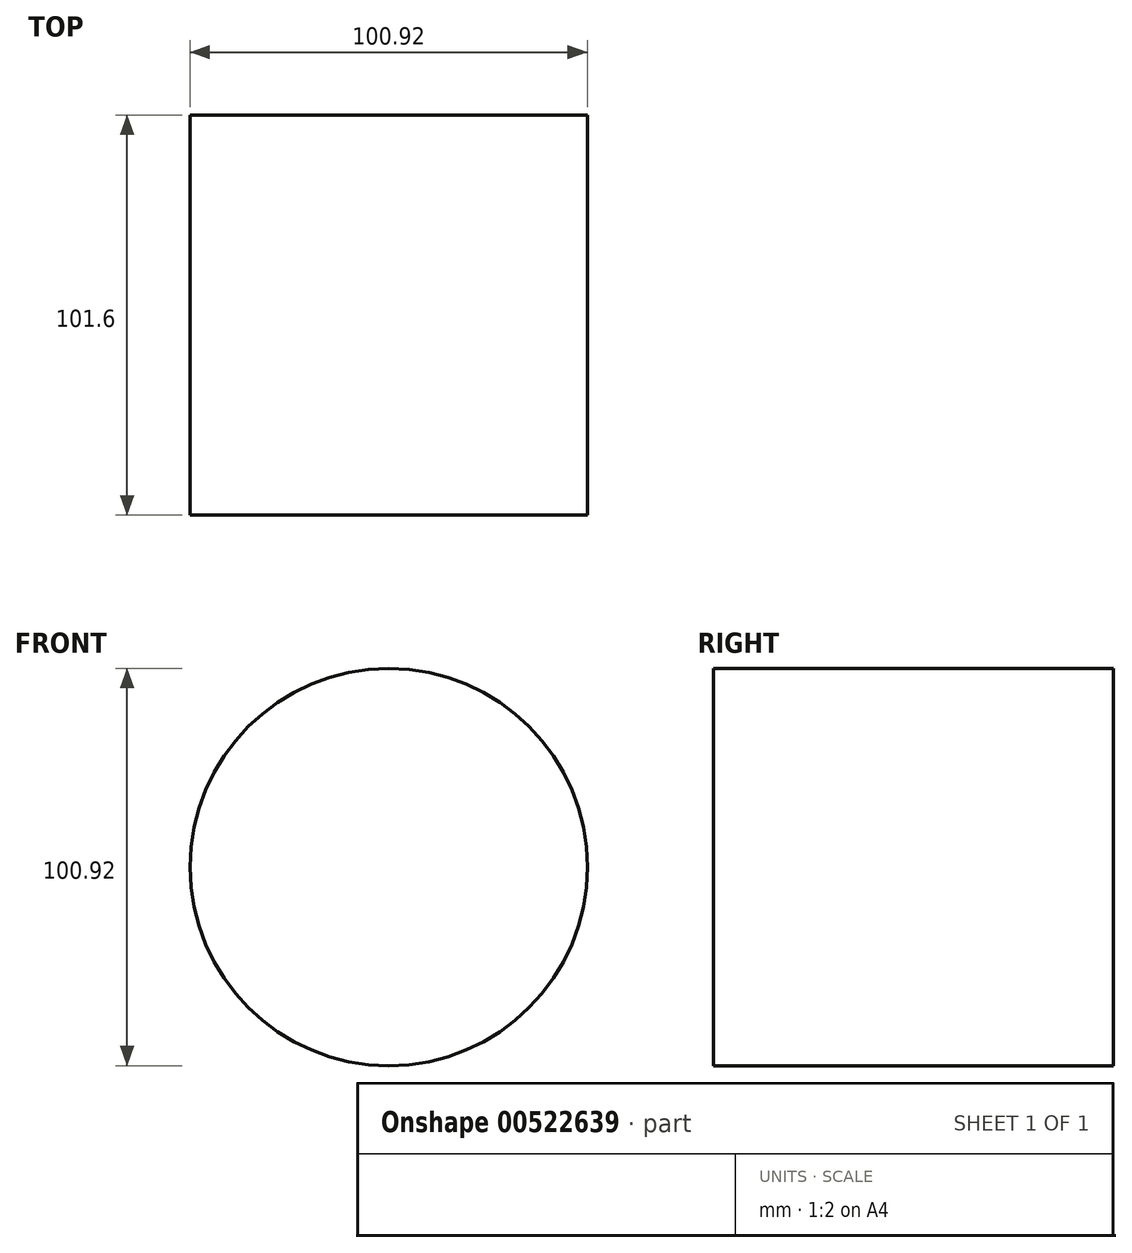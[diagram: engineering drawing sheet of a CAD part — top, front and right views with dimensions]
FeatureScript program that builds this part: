
annotation { "Feature Type Name" : "Feature", "Feature Type Description" : "" }
export const myFeature = defineFeature(function(context is Context, id is Id, definition is map)
    precondition{}
    {
        {
            var Q0;
            Q0=qCreatedBy(makeId("Front.planeOp"),FACE);
            var sketch = newSketch(context, id + "F0", { "sketchPlane" : qUnion([Q0])});
            skCircle(sketch, "E0", {"center": v(0, 0) * mm, "radius": 50.46 * mm});
            skSolve(sketch);
        }
        {
            var Q0;
            Q0 = qSketchRegion(id + "F0", true);
            extrude(context, id + "F1", {"entities" : qUnion([Q0]), "depth" : 101.6 * mm, "offsetDistance" : 25.4 * mm});
        }
    });
